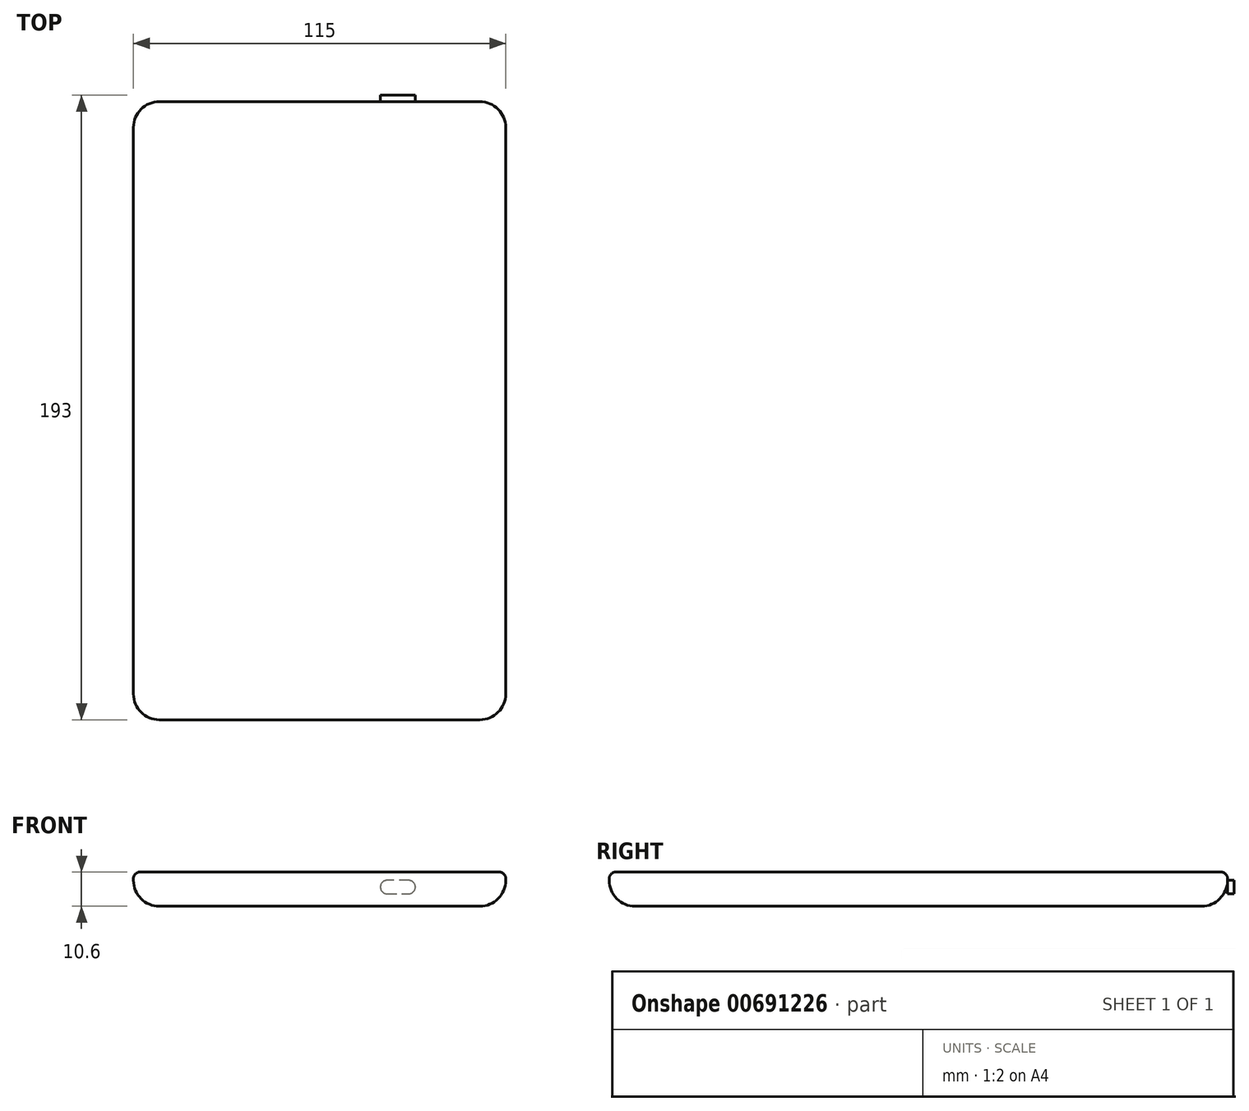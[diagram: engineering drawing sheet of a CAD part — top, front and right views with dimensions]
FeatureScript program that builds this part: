
annotation { "Feature Type Name" : "Feature", "Feature Type Description" : "" }
export const myFeature = defineFeature(function(context is Context, id is Id, definition is map)
    precondition{}
    {
        {
            var Q0;
            Q0=qCreatedBy(makeId("Top.planeOp"),FACE);
            var sketch = newSketch(context, id + "F0", { "sketchPlane" : qUnion([Q0])});
            skLineSegment(sketch, "E0.bottom", {"start": v(57.5, 95.5) * mm, "end": v(-57.5, 95.5) * mm});
            skLineSegment(sketch, "E0.top", {"start": v(57.5, -95.5) * mm, "end": v(-57.5, -95.5) * mm});
            skLineSegment(sketch, "E0.left", {"start": v(57.5, 95.5) * mm, "end": v(57.5, -95.5) * mm});
            skLineSegment(sketch, "E0.right", {"start": v(-57.5, 95.5) * mm, "end": v(-57.5, -95.5) * mm});
            skPoint(sketch, "E0.middle", {"position": v(0, 0) * mm});
            skSolve(sketch);
        }
        {
            var Q0;
            Q0=makeQuery(id+"F0.imprint","IMPRINT",FACE,{"disambiguationData":[TD([[makeQuery(id+"F0.imprint","IMPRINT",EDGE,{"derivedFrom":sQuery(id+"F0.wireOp",EDGE,"E0.bottom")}),1.0]])]});
            extrude(context, id + "F1", {"entities" : qUnion([Q0]), "depth" : 10.6 * mm});
        }
        {
            var Q0;
            Q0=makeQuery(id+"F1.opExtrude","CAP_EDGE",EDGE,{"disambiguationData":[OSD([sQuery(id+"F0.wireOp",EDGE,"E0.right")])],"isStart":true});
            var Q1;
            Q1=makeQuery(id+"F1.opExtrude","CAP_EDGE",EDGE,{"disambiguationData":[OSD([sQuery(id+"F0.wireOp",EDGE,"E0.bottom")])],"isStart":true});
            var Q2;
            Q2=makeQuery(id+"F1.opExtrude","CAP_EDGE",EDGE,{"disambiguationData":[OSD([sQuery(id+"F0.wireOp",EDGE,"E0.left")])],"isStart":true});
            var Q3;
            Q3=makeQuery(id+"F1.opExtrude","CAP_EDGE",EDGE,{"disambiguationData":[OSD([sQuery(id+"F0.wireOp",EDGE,"E0.top")])],"isStart":true});
            var Q4;
            Q4=makeQuery(id+"F1.opExtrude","SWEPT_EDGE",EDGE,{"disambiguationData":[OSD([sQuery(id+"F0.wireOp",EDGE,"E0.bottom"),sQuery(id+"F0.wireOp",EDGE,"E0.right")])]});
            var Q5;
            Q5=makeQuery(id+"F1.opExtrude","SWEPT_EDGE",EDGE,{"disambiguationData":[OSD([sQuery(id+"F0.wireOp",EDGE,"E0.bottom"),sQuery(id+"F0.wireOp",EDGE,"E0.left")])]});
            var Q6;
            Q6=makeQuery(id+"F1.opExtrude","SWEPT_EDGE",EDGE,{"disambiguationData":[OSD([sQuery(id+"F0.wireOp",EDGE,"E0.top"),sQuery(id+"F0.wireOp",EDGE,"E0.left")])]});
            var Q7;
            Q7=makeQuery(id+"F1.opExtrude","SWEPT_EDGE",EDGE,{"disambiguationData":[OSD([sQuery(id+"F0.wireOp",EDGE,"E0.top"),sQuery(id+"F0.wireOp",EDGE,"E0.right")])]});
            fillet(context, id + "F2", {"entities" : qUnion([Q0, Q1, Q2, Q3, Q4, Q5, Q6, Q7]), "radius" : 8 * mm, "tangentPropagation" : true, "allowEdgeOverflow" : false});
        }
        {
            var Q0;
            Q0=makeQuery(id+"F1.opExtrude","CAP_EDGE",EDGE,{"disambiguationData":[OSD([sQuery(id+"F0.wireOp",EDGE,"E0.top")])],"isStart":false});
            fillet(context, id + "F3", {"entities" : qUnion([Q0]), "radius" : 2 * mm, "tangentPropagation" : true, "allowEdgeOverflow" : false});
        }
        {
            var Q0;
            Q0=makeQuery(id+"F1.opExtrude","SWEPT_FACE",FACE,{"disambiguationData":[OSD([sQuery(id+"F0.wireOp",EDGE,"E0.bottom")])]});
            var sketch = newSketch(context, id + "F4", { "sketchPlane" : qUnion([Q0])});
            skLineSegment(sketch, "E1.0", {"start": v(-49.5, 10.6) * mm, "end": v(49.5, 10.6) * mm, "construction": true});
            skPoint(sketch, "E2.0", {"position": v(-57.5, 8.6) * mm});
            skLineSegment(sketch, "E3.bottom", {"start": v(-18.8, 8.45) * mm, "end": v(-29.55, 8.45) * mm});
            skLineSegment(sketch, "E3.top", {"start": v(-18.8, 3.85) * mm, "end": v(-29.55, 3.85) * mm});
            skLineSegment(sketch, "E3.left", {"start": v(-18.8, 8.45) * mm, "end": v(-18.8, 3.85) * mm});
            skLineSegment(sketch, "E3.right", {"start": v(-29.55, 8.45) * mm, "end": v(-29.55, 3.85) * mm});
            skPoint(sketch, "E3.middle", {"position": v(-24.17, 6.15) * mm});
            skSolve(sketch);
        }
        {
            var Q0;
            {var subQ0=sQuery(id+"F4.wireOp",EDGE,"E3.top");Q0=makeQuery(id+"F4.imprint","IMPRINT",FACE,{"disambiguationData":[TD([[makeQuery(id+"F4.imprint","IMPRINT",EDGE,{"derivedFrom":subQ0}),-1.0]])]});}
            extrude(context, id + "F5", {"entities" : qUnion([Q0]), "depth" : 2 * mm});
        }
        {
            var Q0;
            Q0=makeQuery(id+"F5.opExtrude","SWEPT_EDGE",EDGE,{"disambiguationData":[OSD([sQuery(id+"F0.wireOp",EDGE,"E0.bottom"),sQuery(id+"F4.wireOp",EDGE,"E3.left")])]});
            var Q1;
            Q1=makeQuery(id+"F5.opExtrude","SWEPT_EDGE",EDGE,{"disambiguationData":[OSD([sQuery(id+"F4.wireOp",EDGE,"E3.top"),sQuery(id+"F4.wireOp",EDGE,"E3.left")])]});
            var Q2;
            Q2=makeQuery(id+"F5.opExtrude","SWEPT_EDGE",EDGE,{"disambiguationData":[OSD([sQuery(id+"F4.wireOp",EDGE,"E3.top"),sQuery(id+"F4.wireOp",EDGE,"E3.right")])]});
            var Q3;
            Q3=makeQuery(id+"F5.opExtrude","SWEPT_EDGE",EDGE,{"disambiguationData":[OSD([sQuery(id+"F0.wireOp",EDGE,"E0.bottom"),sQuery(id+"F4.wireOp",EDGE,"E3.right")])]});
            fillet(context, id + "F6", {"entities" : qUnion([Q0, Q1, Q2, Q3]), "radius" : 2 * mm, "tangentPropagation" : true, "allowEdgeOverflow" : false});
        }
    });
